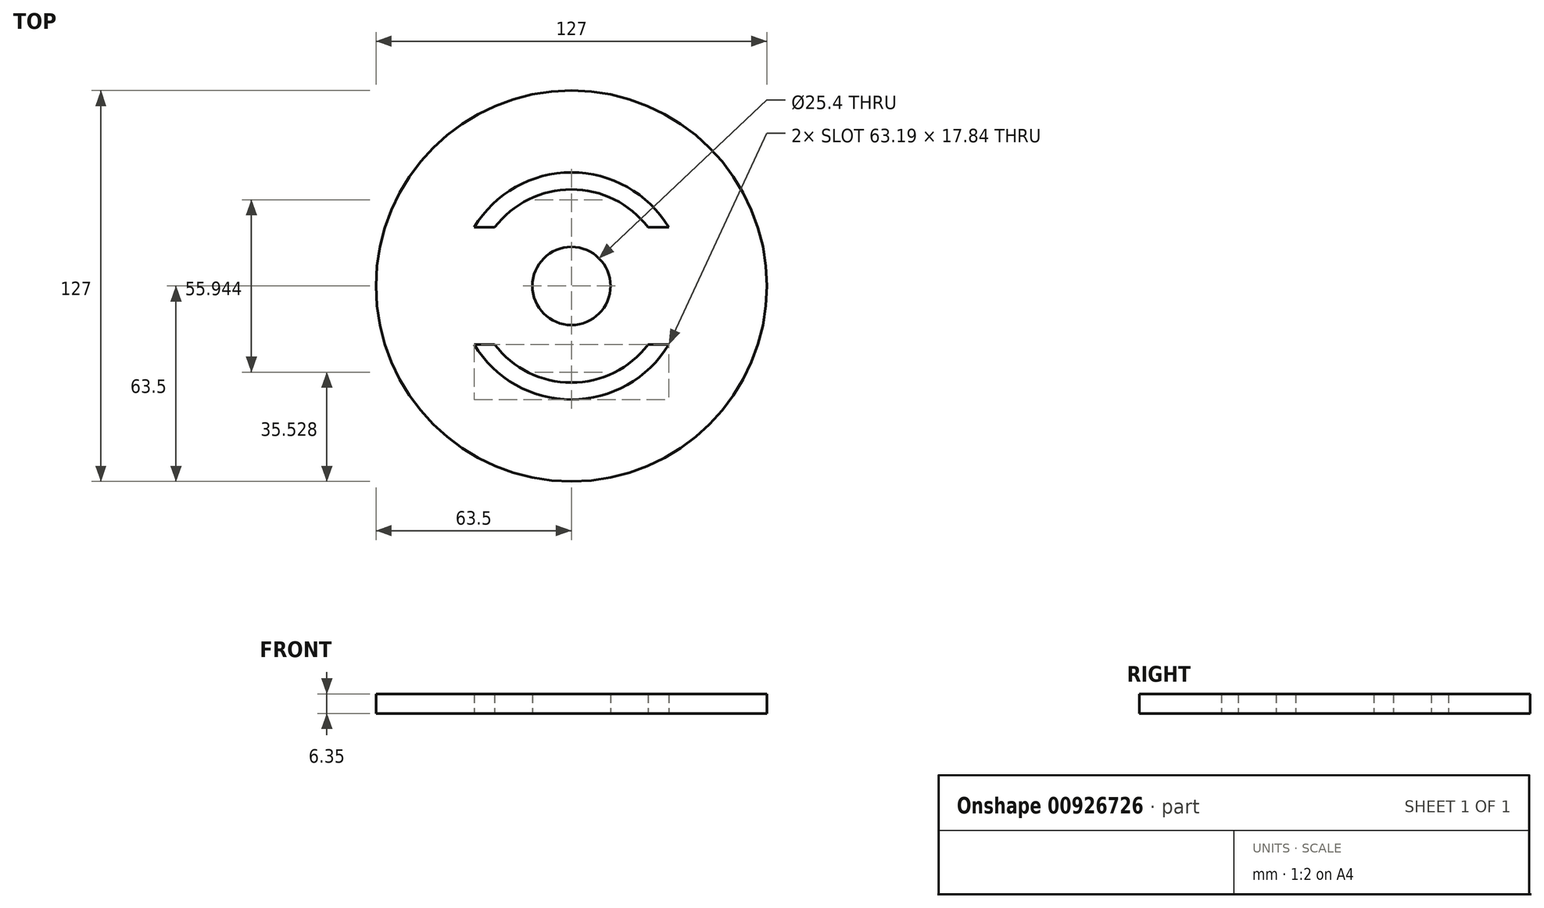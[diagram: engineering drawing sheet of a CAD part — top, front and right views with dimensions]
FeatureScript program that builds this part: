
annotation { "Feature Type Name" : "Feature", "Feature Type Description" : "" }
export const myFeature = defineFeature(function(context is Context, id is Id, definition is map)
    precondition{}
    {
        {
            var Q0;
            Q0=qCreatedBy(makeId("Top.planeOp"),FACE);
            var sketch = newSketch(context, id + "F0", { "sketchPlane" : qUnion([Q0])});
            skArc(sketch, "E0", {"start": v(31.6, 19.05) * mm, "mid": v(0, 36.9) * mm, "end": v(-31.6, 19.05) * mm});
            skArc(sketch, "E1", {"start": v(24.92, 19.05) * mm, "mid": v(0, 31.37) * mm, "end": v(-24.92, 19.05) * mm});
            skCircle(sketch, "E2", {"center": v(0, 0) * mm, "radius": 63.5 * mm});
            skCircle(sketch, "E3", {"center": v(0, 0) * mm, "radius": 12.7 * mm});
            skLineSegment(sketch, "E4", {"start": v(-31.6, 19.05) * mm, "end": v(-24.92, 19.05) * mm});
            skLineSegment(sketch, "E5.trimOffspring", {"start": v(24.92, 19.05) * mm, "end": v(31.6, 19.05) * mm});
            skArc(sketch, "E6.MirrorCS", {"start": v(24.92, -19.05) * mm, "mid": v(0, -31.37) * mm, "end": v(-24.92, -19.05) * mm});
            skLineSegment(sketch, "E7.MirrorCS", {"start": v(-31.6, -19.05) * mm, "end": v(-24.92, -19.05) * mm});
            skArc(sketch, "E8.MirrorCS", {"start": v(31.6, -19.05) * mm, "mid": v(0, -36.9) * mm, "end": v(-31.6, -19.05) * mm});
            skLineSegment(sketch, "E9.MirrorCS", {"start": v(24.92, -19.05) * mm, "end": v(31.6, -19.05) * mm});
            skSolve(sketch);
        }
        {
            var Q0;
            Q0 = qSketchRegion(id + "F0", true);
            extrude(context, id + "F1", {"entities" : qUnion([Q0]), "depth" : 6.35 * mm, "offsetDistance" : 25.4 * mm});
        }
    });
